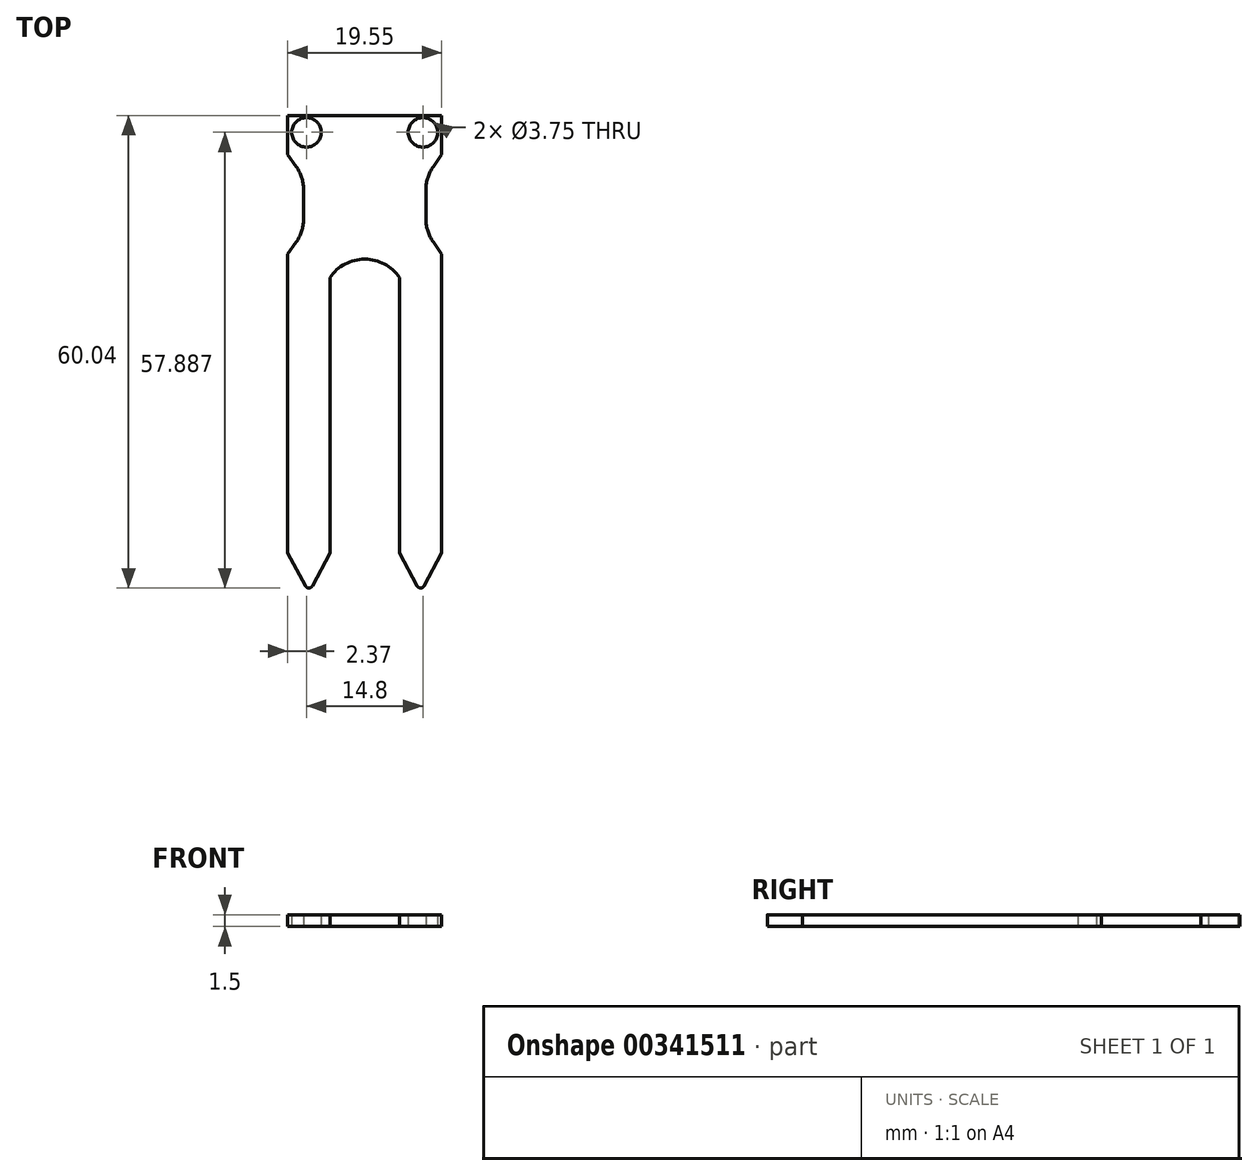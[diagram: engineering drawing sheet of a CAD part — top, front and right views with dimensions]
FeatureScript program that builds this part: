
annotation { "Feature Type Name" : "Feature", "Feature Type Description" : "" }
export const myFeature = defineFeature(function(context is Context, id is Id, definition is map)
    precondition{}
    {
        {
            var Q0;
            Q0=qCreatedBy(makeId("Top.planeOp"),FACE);
            var sketch = newSketch(context, id + "F0", { "sketchPlane" : qUnion([Q0])});
            skLineSegment(sketch, "E0", {"start": v(21, 7.11) * mm, "end": v(18.33, 2.11) * mm});
            skLineSegment(sketch, "E1", {"start": v(18.33, 2.11) * mm, "end": v(15.65, 7.11) * mm});
            skLineSegment(sketch, "E2", {"start": v(21, 45.11) * mm, "end": v(19.94, 46.61) * mm});
            skLineSegment(sketch, "E3", {"start": v(19.01, 49.51) * mm, "end": v(19.01, 53.32) * mm});
            skLineSegment(sketch, "E4", {"start": v(19.94, 56.22) * mm, "end": v(21, 57.71) * mm});
            skLineSegment(sketch, "E5", {"start": v(21, 57.71) * mm, "end": v(21, 62.71) * mm});
            skLineSegment(sketch, "E6", {"start": v(21, 45.11) * mm, "end": v(21, 42.11) * mm});
            skLineSegment(sketch, "E7", {"start": v(21, 42.11) * mm, "end": v(21, 7.11) * mm});
            skLineSegment(sketch, "E8", {"start": v(15.65, 7.11) * mm, "end": v(15.65, 42.11) * mm});
            skLineSegment(sketch, "E9.MirrorCS", {"start": v(1.46, 57.71) * mm, "end": v(1.46, 62.71) * mm});
            skLineSegment(sketch, "E10.MirrorCS", {"start": v(2.52, 56.22) * mm, "end": v(1.46, 57.71) * mm});
            skLineSegment(sketch, "E11.MirrorCS", {"start": v(3.45, 49.51) * mm, "end": v(3.45, 53.32) * mm});
            skLineSegment(sketch, "E12.MirrorCS", {"start": v(1.46, 45.11) * mm, "end": v(2.52, 46.61) * mm});
            skLineSegment(sketch, "E13.MirrorCS", {"start": v(1.46, 42.11) * mm, "end": v(1.46, 7.11) * mm});
            skLineSegment(sketch, "E14.MirrorCS", {"start": v(6.81, 7.11) * mm, "end": v(6.81, 42.11) * mm});
            skLineSegment(sketch, "E15.MirrorCS", {"start": v(1.46, 45.11) * mm, "end": v(1.46, 42.11) * mm});
            skLineSegment(sketch, "E16.MirrorCS", {"start": v(4.13, 2.11) * mm, "end": v(6.81, 7.11) * mm});
            skLineSegment(sketch, "E17.MirrorCS", {"start": v(1.46, 7.11) * mm, "end": v(4.13, 2.11) * mm});
            skLineSegment(sketch, "E18", {"start": v(1.46, 62.71) * mm, "end": v(21, 62.71) * mm});
            skArc(sketch, "E19", {"start": v(15.65, 42.11) * mm, "mid": v(11.23, 44.44) * mm, "end": v(6.81, 42.11) * mm});
            skCircle(sketch, "E20", {"center": v(3.83, 60.56) * mm, "radius": 1.88 * mm});
            skCircle(sketch, "E21", {"center": v(18.63, 60.56) * mm, "radius": 1.88 * mm});
            skPoint(sketch, "E22.visualSharp", {"position": v(19.01, 54.91) * mm});
            skArc(sketch, "E22.filletArc", {"start": v(19.94, 56.22) * mm, "mid": v(19.25, 54.84) * mm, "end": v(19.01, 53.32) * mm});
            skPoint(sketch, "E23.visualSharp", {"position": v(19.01, 47.91) * mm});
            skArc(sketch, "E23.filletArc", {"start": v(19.01, 49.51) * mm, "mid": v(19.25, 47.99) * mm, "end": v(19.94, 46.61) * mm});
            skPoint(sketch, "E24.visualSharp", {"position": v(3.45, 47.91) * mm});
            skArc(sketch, "E24.filletArc", {"start": v(2.52, 46.61) * mm, "mid": v(3.2, 47.99) * mm, "end": v(3.45, 49.51) * mm});
            skPoint(sketch, "E25.visualSharp", {"position": v(3.45, 54.91) * mm});
            skArc(sketch, "E25.filletArc", {"start": v(3.45, 53.32) * mm, "mid": v(3.2, 54.84) * mm, "end": v(2.52, 56.22) * mm});
            skSolve(sketch);
        }
        {
            var Q0;
            Q0 = qSketchRegion(id + "F0", true);
            extrude(context, id + "F1", {"entities" : qUnion([Q0]), "depth" : 1.5 * mm});
        }
        {
            var Q0;
            Q0=makeQuery(id+"F1.opExtrude","SWEPT_EDGE",EDGE,{"disambiguationData":[OSD([sQuery(id+"F0.wireOp",EDGE,"E0"),sQuery(id+"F0.wireOp",EDGE,"E1")])]});
            var Q1;
            Q1=makeQuery(id+"F1.opExtrude","SWEPT_EDGE",EDGE,{"disambiguationData":[OSD([sQuery(id+"F0.wireOp",EDGE,"E16.MirrorCS"),sQuery(id+"F0.wireOp",EDGE,"E17.MirrorCS")])]});
            fillet(context, id + "F2", {"entities" : qUnion([Q0, Q1]), "radius" : .5 * mm, "tangentPropagation" : true, "allowEdgeOverflow" : false});
        }
    });
